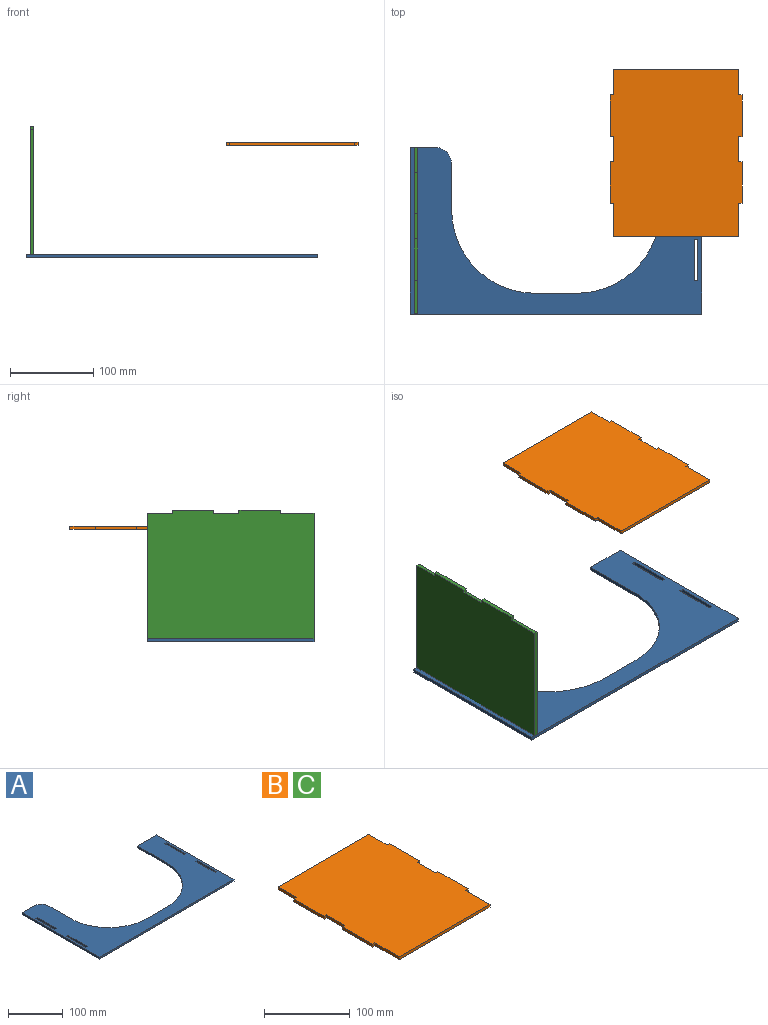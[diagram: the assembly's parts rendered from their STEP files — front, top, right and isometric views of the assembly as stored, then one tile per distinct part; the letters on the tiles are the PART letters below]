
ASSEMBLY  parts=3 mates=1
PART A: 29 faces, bbox 350x200x4 mm
  f0: plane 350x200mm, normal (0,0,1), area 29636.2mm2, adj f2,f3,f4,f5,f6,f7,f8,f9
  f1: plane 350x200mm, normal (0,0,-1), area 29636.2mm2, adj f2,f3,f4,f5,f6,f7,f8,f9
  f2: plane 30x4mm, normal (0,1,0), area 120mm2, adj f0,f1,f3,f7
  f3: plane 200x4mm, normal (-1,0,0), area 800mm2, adj f0,f1,f2,f4
  f4: plane 350x4mm, normal (0,-1,0), area 1400mm2, adj f0,f1,f3,f10
  f5: plane 50x4mm, normal (0,1,0), area 200mm2, adj f0,f1,f8,f12
  f6: plane 55x4mm, normal (1,0,0), area 220mm2, adj f0,f1,f7,f8
  f7: cylinder r=20mm len=20mm, axis (0,0,-1), area 125.7mm2, adj f0,f1,f2,f6
  f8: cylinder r=100mm len=100mm, axis (0,0,1), area 628.3mm2, adj f0,f1,f5,f6
  f9: plane 50x4mm, normal (0,1,0), area 200mm2, adj f0,f1,f10,f11
  f10: plane 200x4mm, normal (1,0,0), area 800mm2, adj f0,f1,f4,f9
  f11: plane 75x4mm, normal (-1,0,0), area 300mm2, adj f0,f1,f9,f12
  f12: cylinder r=100mm len=100mm, axis (0,0,1), area 628.3mm2, adj f0,f1,f5,f11
  f13: plane 4.1x4mm, normal (0,-1,0), area 16.4mm2, adj f0,f1,f14,f16
  f14: plane 50x4mm, normal (-1,0,0), area 200mm2, adj f0,f1,f13,f15
  f15: plane 4.1x4mm, normal (0,1,0), area 16.4mm2, adj f0,f1,f14,f16
  f16: plane 50x4mm, normal (1,0,0), area 200mm2, adj f0,f1,f13,f15
  f17: plane 4.1x4mm, normal (0,-1,0), area 16.4mm2, adj f0,f1,f18,f20
  f18: plane 50x4mm, normal (-1,0,0), area 200mm2, adj f0,f1,f17,f19
  f19: plane 4.1x4mm, normal (0,1,0), area 16.4mm2, adj f0,f1,f18,f20
  f20: plane 50x4mm, normal (1,0,0), area 200mm2, adj f0,f1,f17,f19
  f21: plane 4.1x4mm, normal (0,1,0), area 16.4mm2, adj f0,f1,f22,f24
  f22: plane 50x4mm, normal (-1,0,0), area 200mm2, adj f0,f1,f21,f23
  f23: plane 4.1x4mm, normal (0,-1,0), area 16.4mm2, adj f0,f1,f22,f24
  f24: plane 50x4mm, normal (1,0,0), area 200mm2, adj f0,f1,f21,f23
  f25: plane 4.1x4mm, normal (0,1,0), area 16.4mm2, adj f0,f1,f26,f28
  f26: plane 50x4mm, normal (-1,0,0), area 200mm2, adj f0,f1,f25,f27
  f27: plane 4.1x4mm, normal (0,-1,0), area 16.4mm2, adj f0,f1,f26,f28
  f28: plane 50x4mm, normal (1,0,0), area 200mm2, adj f0,f1,f25,f27
PART B: 22 faces, bbox 158x200x4 mm
  f0: plane 30x4mm, normal (1,0,0), area 120mm2, adj f8,f9,f18,f20
  f1: plane 40x4mm, normal (1,0,0), area 160mm2, adj f6,f8,f9,f16
  f2: plane 40x4mm, normal (-1,0,0), area 160mm2, adj f6,f8,f9,f15
  f3: plane 30x4mm, normal (-1,0,0), area 120mm2, adj f8,f9,f12,f13
  f4: plane 150x4mm, normal (0,1,0), area 600mm2, adj f5,f7,f8,f9
  f5: plane 30x4mm, normal (-1,0,0), area 120mm2, adj f4,f8,f9,f10
  f6: plane 150x4mm, normal (0,-1,0), area 600mm2, adj f1,f2,f8,f9
  f7: plane 30x4mm, normal (1,0,0), area 120mm2, adj f4,f8,f9,f19
  f8: plane 200x158mm, normal (0,0,1), area 30800mm2, adj f0,f1,f2,f3,f4,f5,f6,f7
  f9: plane 200x158mm, normal (0,0,-1), area 30800mm2, adj f0,f1,f2,f3,f4,f5,f6,f7
  f10: plane 4x4mm, normal (0,1,0), area 16mm2, adj f5,f8,f9,f11
  f11: plane 50x4mm, normal (-1,0,0), area 200mm2, adj f8,f9,f10,f12
  f12: plane 4x4mm, normal (0,-1,0), area 16mm2, adj f3,f8,f9,f11
  f13: plane 4x4mm, normal (0,1,0), area 16mm2, adj f3,f8,f9,f14
  f14: plane 50x4mm, normal (-1,0,0), area 200mm2, adj f8,f9,f13,f15
  f15: plane 4x4mm, normal (0,-1,0), area 16mm2, adj f2,f8,f9,f14
  f16: plane 4x4mm, normal (0,-1,0), area 16mm2, adj f1,f8,f9,f17
  f17: plane 50x4mm, normal (1,0,0), area 200mm2, adj f8,f9,f16,f18
  f18: plane 4x4mm, normal (0,1,0), area 16mm2, adj f0,f8,f9,f17
  f19: plane 4x4mm, normal (0,1,0), area 16mm2, adj f7,f8,f9,f21
  f20: plane 4x4mm, normal (0,-1,0), area 16mm2, adj f0,f8,f9,f21
  f21: plane 50x4mm, normal (1,0,0), area 200mm2, adj f8,f9,f19,f20
PART C: same geometry as B
PLACE A t=(-34.75,-15.53,3.24)mm
PLACE B t=(209.48,77.15,138.11)mm
PLACE C rot(axis=(0,-1,0),90deg) t=(-25.75,-15.53,7.24)mm
MATE fastened C.f11 <-> A.f1  axis (0,0,-1) through (-29.75,154.47,3.24)mm
